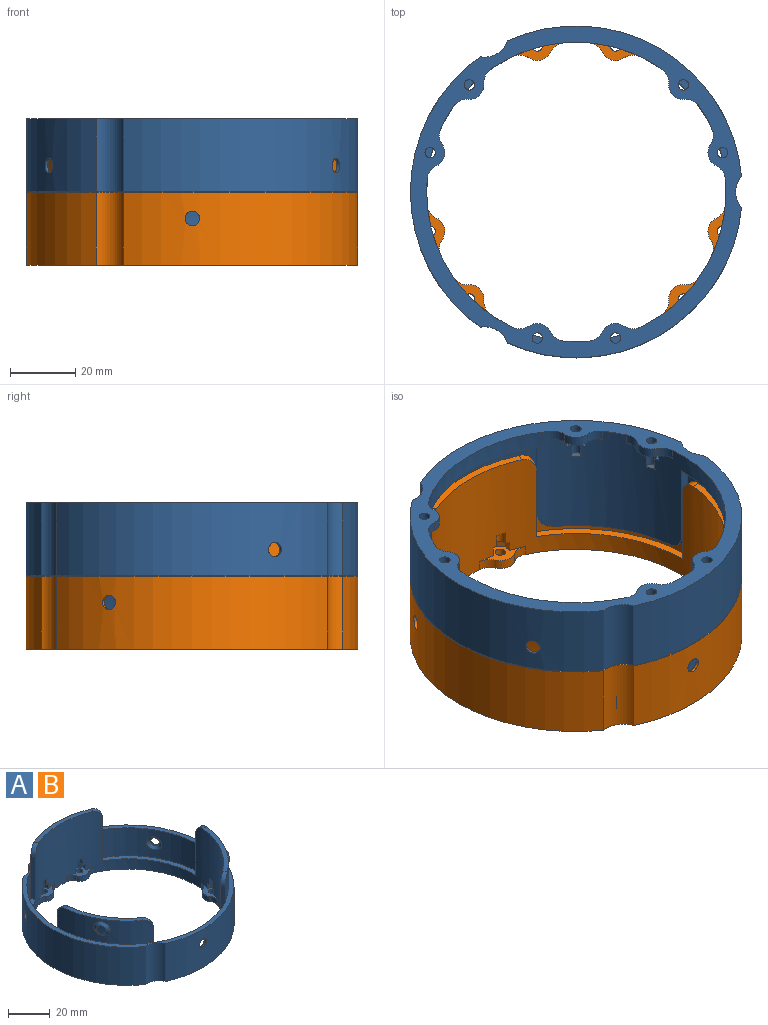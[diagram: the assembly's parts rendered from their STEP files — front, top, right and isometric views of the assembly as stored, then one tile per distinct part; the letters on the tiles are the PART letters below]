
ASSEMBLY  parts=2 mates=1
PART A: 117 faces, bbox 101.8x102.9x36 mm
  f0: cylinder r=51mm len=71.96mm, axis (0,0,-1), area 2159.6mm2, adj f6,f14,f21,f35,f44
  f1: cylinder r=51mm len=83.1mm, axis (0,0,-1), area 2159.6mm2, adj f6,f7,f14,f21,f43
  f2: cylinder r=51mm len=71.96mm, axis (0,0,-1), area 2159.6mm2, adj f7,f14,f21,f35,f42
  f3: bspline ~8.47x7.34mm, area 41.6mm2, adj f23,f44
  f4: bspline ~8.47x7.34mm, area 41.6mm2, adj f30,f43
  f5: bspline ~8.47x8.47mm, area 41.6mm2, adj f8,f42
  f6: cylinder r=7.5mm len=22.4mm, axis (0,0,-1), area 235.6mm2, adj f0,f1,f14,f21
  f7: cylinder r=7.5mm len=22.4mm, axis (0,0,-1), area 235.6mm2, adj f1,f2,f14,f21
  f8: cylinder r=48.6mm len=48.97mm, axis (0,0,1), area 796.2mm2, adj f5,f14,f27,f28,f29
  f9: cylinder r=49.81mm len=5mm, axis (0,0,1), area 19.6mm2, adj f10
  f10: bspline ~8.03x6.95mm, area 42.1mm2, adj f9,f16
  f11: cylinder r=49.81mm len=5mm, axis (0,0,1), area 19.6mm2, adj f12
  f12: bspline ~8.03x6.95mm, area 42.1mm2, adj f11,f22
  f13: bspline ~8.03x8.03mm, area 42.1mm2, adj f15,f34
  f14: plane 102x101.77mm, normal (0,0,1), area 741.6mm2, adj f0,f1,f2,f6,f7,f8,f15,f16
  f15: cylinder r=48.4mm len=48.03mm, axis (0,0,-1), area 623.4mm2, adj f13,f14,f19,f24,f31,f37,f41
  f16: cylinder r=48.4mm len=41.6mm, axis (0,0,-1), area 623.4mm2, adj f10,f14,f17,f27,f32,f36,f38
  f17: plane 33.87x20.76mm, normal (0,0,1), area 93.6mm2, adj f16,f20,f36,f38
  f18: plane 33.87x20.76mm, normal (0,0,1), area 93.6mm2, adj f20,f22,f39,f40
  f19: plane 39.09x6.22mm, normal (0,0,1), area 93.6mm2, adj f15,f20,f37,f41
  f20: cylinder r=46mm len=92mm, axis (0,0,-1), area 5532.7mm2, adj f17,f18,f19,f21,f24,f25,f26,f27
  f21: plane 102x101.77mm, normal (0,0,-1), area 1617.1mm2, adj f0,f1,f2,f6,f7,f20,f35,f46
  f22: cylinder r=48.4mm len=41.6mm, axis (0,0,-1), area 623.4mm2, adj f12,f14,f18,f25,f28,f39,f40
  f23: cylinder r=48.6mm len=42.41mm, axis (0,0,1), area 796.2mm2, adj f3,f14,f24,f25,f26
  f24: plane 25x2.26mm, normal (0.87,-0.5,0), area 63.3mm2, adj f14,f15,f20,f23,f26,f41
  f25: plane 25x2.6mm, normal (0,1,0), area 63.3mm2, adj f14,f20,f22,f23,f26,f40
  f26: plane 42.41x25.77mm, normal (0,0,1), area 129.9mm2, adj f20,f23,f24,f25
  f27: plane 25x2.25mm, normal (0.86,-0.5,0), area 63.3mm2, adj f8,f14,f16,f20,f29,f38
  f28: plane 25x2.25mm, normal (-0.86,-0.5,0), area 63.3mm2, adj f8,f14,f20,f22,f29,f39
  f29: plane 48.97x8.86mm, normal (0,0,1), area 129.9mm2, adj f8,f20,f27,f28
  f30: cylinder r=48.6mm len=42.41mm, axis (0,0,1), area 796.2mm2, adj f4,f14,f31,f32,f33
  f31: plane 25x2.26mm, normal (-0.87,-0.5,0), area 63.3mm2, adj f14,f15,f20,f30,f33,f37
  f32: plane 25x2.6mm, normal (0,1,0), area 63.3mm2, adj f14,f16,f20,f30,f33,f36
  f33: plane 42.41x25.77mm, normal (0,0,1), area 129.9mm2, adj f20,f30,f31,f32
  f34: cylinder r=49.81mm len=5mm, axis (0,0,1), area 19.6mm2, adj f13
  f35: cylinder r=7.5mm len=22.4mm, axis (0,0,-1), area 235.6mm2, adj f0,f2,f14,f21
  f36: cylinder r=5mm len=5.01mm, axis (1,0,0), area 18.9mm2, adj f16,f17,f20,f32
  f37: cylinder r=5mm len=5.67mm, axis (-0.5,0.87,0), area 18.9mm2, adj f15,f19,f20,f31
  f38: cylinder r=5mm len=5.67mm, axis (-0.5,-0.86,0), area 18.9mm2, adj f16,f17,f20,f27
  f39: cylinder r=5mm len=5.67mm, axis (-0.5,0.86,0), area 18.9mm2, adj f18,f20,f22,f28
  f40: cylinder r=5mm len=5.01mm, axis (1,0,0), area 18.9mm2, adj f18,f20,f22,f25
  f41: cylinder r=5mm len=5.67mm, axis (-0.5,-0.87,0), area 18.9mm2, adj f15,f19,f20,f24
  f42: cylinder r=2.25mm len=4.5mm, axis (0,1,0), area 12mm2, adj f2,f5
  f43: cylinder r=2.25mm len=4.5mm, axis (0.87,-0.5,0), area 12mm2, adj f1,f4
  f44: cylinder r=2.25mm len=4.5mm, axis (-0.87,-0.5,0), area 12mm2, adj f0,f3
  f45: plane 15.67x7.67mm, normal (0,0,1), area 39.3mm2, adj f20,f46,f68,f69,f70,f71,f104,f115
  f46: cylinder r=4.49mm len=6.61mm, axis (0,0,-1), area 23.3mm2, adj f21,f45,f115,f116
  f47: plane 15.67x7.67mm, normal (0,0,1), area 39.3mm2, adj f20,f48,f58,f59,f60,f61,f103,f113
  f48: cylinder r=4.49mm len=6.61mm, axis (0,0,-1), area 23.3mm2, adj f21,f47,f113,f114
  f49: plane 11.47x11.47mm, normal (0,0,1), area 39.3mm2, adj f20,f50,f78,f79,f80,f81,f102,f111
  f50: cylinder r=4.49mm len=4.85mm, axis (0,0,-1), area 23.3mm2, adj f21,f49,f111,f112
  f51: plane 15.67x7.67mm, normal (0,0,1), area 39.3mm2, adj f20,f52,f73,f74,f75,f76,f101,f109
  f52: cylinder r=4.49mm len=6.61mm, axis (0,0,-1), area 23.3mm2, adj f21,f51,f109,f110
  f53: plane 15.67x7.67mm, normal (0,0,1), area 39.3mm2, adj f20,f54,f83,f84,f85,f86,f100,f107
  f54: cylinder r=4.49mm len=6.61mm, axis (0,0,-1), area 23.3mm2, adj f21,f53,f107,f108
  f55: plane 11.47x11.47mm, normal (0,0,1), area 39.3mm2, adj f20,f56,f63,f64,f65,f66,f99,f105
  f56: cylinder r=4.49mm len=4.85mm, axis (0,0,-1), area 23.3mm2, adj f21,f55,f105,f106
  f57: plane 6.09x4.49mm, normal (0,0,-1), area 11.5mm2, adj f20,f58,f59,f60,f61,f97
  f58: plane 3x2.17mm, normal (-0.97,-0.26,0), area 6.7mm2, adj f20,f47,f57,f61
  f59: plane 3x2.17mm, normal (0.97,0.26,0), area 6.7mm2, adj f20,f47,f57,f60
  f60: plane 3x2.33mm, normal (0.71,-0.71,0), area 9.9mm2, adj f47,f57,f59,f61
  f61: plane 3.18x3mm, normal (-0.26,-0.97,0), area 9.9mm2, adj f47,f57,f58,f60
  f62: plane 5.62x5.62mm, normal (0,0,-1), area 11.5mm2, adj f20,f63,f64,f65,f66,f95
  f63: plane 3x1.59mm, normal (0.71,-0.71,0), area 6.7mm2, adj f20,f55,f62,f65
  f64: plane 3x1.59mm, normal (-0.71,0.71,0), area 6.7mm2, adj f20,f55,f62,f66
  f65: plane 3.18x3mm, normal (0.97,0.26,0), area 9.9mm2, adj f55,f62,f63,f66
  f66: plane 3.18x3mm, normal (0.26,0.97,0), area 9.9mm2, adj f55,f62,f64,f65
  f67: plane 6.09x4.49mm, normal (0,0,-1), area 11.5mm2, adj f20,f68,f69,f70,f71,f93
  f68: plane 3x2.17mm, normal (-0.97,0.26,0), area 6.7mm2, adj f20,f45,f67,f71
  f69: plane 3x2.17mm, normal (0.97,-0.26,0), area 6.7mm2, adj f20,f45,f67,f70
  f70: plane 3.18x3mm, normal (0.26,-0.97,0), area 9.9mm2, adj f45,f67,f69,f71
  f71: plane 3x2.33mm, normal (-0.71,-0.71,0), area 9.9mm2, adj f45,f67,f68,f70
  f72: plane 6.09x4.49mm, normal (0,0,-1), area 11.5mm2, adj f20,f73,f74,f75,f76,f91
  f73: plane 3x2.17mm, normal (0.26,0.97,0), area 6.7mm2, adj f20,f51,f72,f75
  f74: plane 3x2.17mm, normal (-0.26,-0.97,0), area 6.7mm2, adj f20,f51,f72,f76
  f75: plane 3x2.33mm, normal (-0.71,0.71,0), area 9.9mm2, adj f51,f72,f73,f76
  f76: plane 3.18x3mm, normal (-0.97,-0.26,0), area 9.9mm2, adj f51,f72,f74,f75
  f77: plane 5.62x5.62mm, normal (0,0,-1), area 11.5mm2, adj f20,f78,f79,f80,f81,f89
  f78: plane 3x1.59mm, normal (0.71,0.71,0), area 6.7mm2, adj f20,f49,f77,f81
  f79: plane 3x1.59mm, normal (-0.71,-0.71,0), area 6.7mm2, adj f20,f49,f77,f80
  f80: plane 3.18x3mm, normal (-0.97,0.26,0), area 9.9mm2, adj f49,f77,f79,f81
  f81: plane 3.18x3mm, normal (-0.26,0.97,0), area 9.9mm2, adj f49,f77,f78,f80
  f82: plane 6.09x4.49mm, normal (0,0,-1), area 11.5mm2, adj f20,f83,f84,f85,f86,f87
  f83: plane 3x2.17mm, normal (0.26,-0.97,0), area 6.7mm2, adj f20,f53,f82,f86
  f84: plane 3x2.17mm, normal (-0.26,0.97,0), area 6.7mm2, adj f20,f53,f82,f85
  f85: plane 3x2.33mm, normal (0.71,0.71,0), area 9.9mm2, adj f53,f82,f84,f86
  f86: plane 3.18x3mm, normal (0.97,-0.26,0), area 9.9mm2, adj f53,f82,f83,f85
  f87: cylinder r=1.6mm len=4mm, axis (0,0,-1), area 24.5mm2, adj f20,f82,f88
  f88: plane 3.2x2.51mm, normal (0,0,-1), area 5.6mm2, adj f20,f87
  f89: cylinder r=1.6mm len=4mm, axis (0,0,-1), area 24.5mm2, adj f20,f77,f90
  f90: plane 3.04x3.04mm, normal (0,0,-1), area 5.6mm2, adj f20,f89
  f91: cylinder r=1.6mm len=4mm, axis (0,0,-1), area 24.5mm2, adj f20,f72,f92
  f92: plane 3.2x2.51mm, normal (0,0,-1), area 5.6mm2, adj f20,f91
  f93: cylinder r=1.6mm len=4mm, axis (0,0,-1), area 24.5mm2, adj f20,f67,f94
  f94: plane 3.2x2.51mm, normal (0,0,-1), area 5.6mm2, adj f20,f93
  f95: cylinder r=1.6mm len=4mm, axis (0,0,-1), area 24.5mm2, adj f20,f62,f96
  f96: plane 3.04x3.04mm, normal (0,0,-1), area 5.6mm2, adj f20,f95
  f97: cylinder r=1.6mm len=4mm, axis (0,0,-1), area 24.5mm2, adj f20,f57,f98
  f98: plane 3.2x2.51mm, normal (0,0,-1), area 5.6mm2, adj f20,f97
  f99: cylinder r=1.6mm len=3.2mm, axis (0,0,-1), area 30.2mm2, adj f21,f55
  f100: cylinder r=1.6mm len=3.2mm, axis (0,0,-1), area 30.2mm2, adj f21,f53
  f101: cylinder r=1.6mm len=3.2mm, axis (0,0,-1), area 30.2mm2, adj f21,f51
  f102: cylinder r=1.6mm len=3.2mm, axis (0,0,-1), area 30.2mm2, adj f21,f49
  f103: cylinder r=1.6mm len=3.2mm, axis (0,0,-1), area 30.2mm2, adj f21,f47
  f104: cylinder r=1.6mm len=3.2mm, axis (0,0,-1), area 30.2mm2, adj f21,f45
  f105: cylinder r=5mm len=4.5mm, axis (0,0,-1), area 15.6mm2, adj f20,f21,f55,f56
  f106: cylinder r=5mm len=4.5mm, axis (0,0,1), area 15.6mm2, adj f20,f21,f55,f56
  f107: cylinder r=5mm len=4.09mm, axis (0,0,-1), area 15.6mm2, adj f20,f21,f53,f54
  f108: cylinder r=5mm len=4.96mm, axis (0,0,1), area 15.6mm2, adj f20,f21,f53,f54
  f109: cylinder r=5mm len=4.96mm, axis (0,0,-1), area 15.6mm2, adj f20,f21,f51,f52
  f110: cylinder r=5mm len=4.09mm, axis (0,0,1), area 15.6mm2, adj f20,f21,f51,f52
  f111: cylinder r=5mm len=4.5mm, axis (0,0,-1), area 15.6mm2, adj f20,f21,f49,f50
  f112: cylinder r=5mm len=4.5mm, axis (0,0,1), area 15.6mm2, adj f20,f21,f49,f50
  f113: cylinder r=5mm len=4.09mm, axis (0,0,-1), area 15.6mm2, adj f20,f21,f47,f48
  f114: cylinder r=5mm len=4.96mm, axis (0,0,1), area 15.6mm2, adj f20,f21,f47,f48
  f115: cylinder r=5mm len=4.96mm, axis (0,0,-1), area 15.6mm2, adj f20,f21,f45,f46
  f116: cylinder r=5mm len=4.09mm, axis (0,0,1), area 15.6mm2, adj f20,f21,f45,f46
PART B: same geometry as A
PLACE A rot(axis=(1,0,0),180deg) t=(0,0,45)mm
PLACE B at identity
MATE fastened B.f8 <-> A.f8  axis (0,0,1) through (0,0,22.4)mm
